# Revit family: PRD_AR_ShwrMxrs_SelfClosingShowerValve_F3SV2005
name_source: partatom
category: Plumbing Fixtures
revit_build: Autodesk Revit 2018 (Build: 20190510_1515(x64)
units: mm (PartAtom-declared; Revit-internal decimal feet)

## family parameters
Cut with Voids When Loaded = Yes
Host = Face
OmniClass Number = 23.45.05.14.99
OmniClass Title = Other Sanitary Washing Plumbing Fixtures
Part Type = Normal
Room Calculation Point = No
Round Connector Dimension = Use Diameter
Shared = No

## types (1)
- F3SV2005 with instalation kit F3BV2001
    AssetType = Fixed
    BIMObjectName = PRD_AR_ShowerManualWaterSupplySets_SelfClosingShowerValve_F3SV2005
    BodyMaterial = Brass
    CasingMaterial = PRD_AR_StainlessSteel_SatinFinished
    Category = Pr_40_20_87_78, Shower manual water supply sets
    CloseOffRating = 0
    Color = Chrome
    Default Elevation = 1000 mm  [stored 3.28084 ft]
    Description = F3S self-closing straight-way valve DN 15 as finished installation kit for installation in basic installation kit, for shower facilities. Self-closing functional part, hydraulically controlled, piston-free design, self-closing, stepless adjustment of flow duration. For connection to pre-mixed hot water or cold water. Housing including changeable valve seat, visible parts, high-polished chromium-plated brass. Holding frame including profile seal, stainless steel cover plate 190 x 245 mm with covered screw fixing and rosette. Depth adjustability 20 mm.
    DiameterNominal = 15  [stored 0.0492126 ft]
    DurationUnit = year
    Finish = Chromised
    FittingMaterial = PRD_AR_ChromatedBrass_HighPolished
    Flow = 0.2 L/s
    FlowCoefficient = 0
    FunctionalPrinciple = HYDRALIC-C
    GrossWeight = 1.50 kg
    IfcExportAs = IfcValveType
    IfcExportType = MIXING
    Manufacturer = KWC Group AG
    ManufacturerName = KWC Group AG
    ManufacturerURL = www.kwc.com
    Material = Brass
    MaterialsBody = Brass
    MaterialsFinishAndColour = Chrome
    MaximumFlowTime = 35s
    MinimumFlowPressure = 1.00 bar
    MinimumFlowTime = 5s
    MixerControl = Other
    Model = F3SV2005
    ModelNumber = 2030040072
    ModelReference = F3SV2005
    NBSDescription = Shower mixers
    NBSReference = 45-35-70/335
    Name = F3 Self closing shower valve F3SV2005
    NetWeight = 1.30 kg
    NominalHeight = 0 mm  [stored 0 ft]
    NominalLength = 0 mm  [stored 0 ft]
    NominalWidth = 0 mm  [stored 0 ft]
    OutletConnectionSize = 15  [stored 0.0492126 ft]
    PositionOfWaterConnection = bottom
    ProductInformation = https://pim.kwc.com
    Size = 15 mm  [stored 0.0492126 ft]
    TestPressure = 0
    TypeOfMounting = In-Wall-Installation-With-Box
    TypeOfShower = In-Wall-Fitting
    URL = www.kwc.com
    Uniclass2015Code = Pr_40_20_87_78
    Uniclass2015Title = Shower manual water supply sets
    Uniclass2015Version = Products v1.10
    ValveMechanism = Other
    ValveOperation = Other
    Version = 1
    VolumeFlowRateAt3Bar = 0.20 L/s
    WarrantyDurationUnit = year

note: [stored X ft] marks values corroborated as IEEE doubles in the binary element streams (Revit-internal decimal feet)

## geometry (parser evidence)
native form markers: Sweep x3
no freeform markers — native parametric forms only
